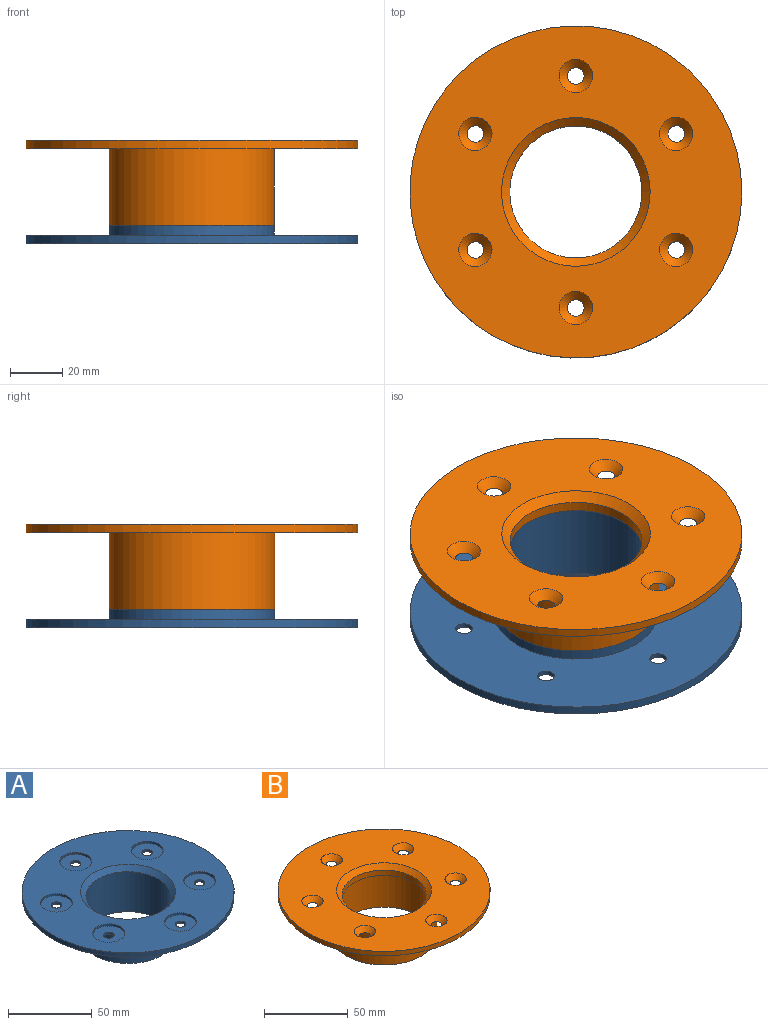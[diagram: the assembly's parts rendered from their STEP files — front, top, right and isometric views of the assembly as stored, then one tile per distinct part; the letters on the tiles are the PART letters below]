
ASSEMBLY  parts=2 mates=1
PART A: 27 faces, bbox 126.5x126.5x32.4 mm
  f0: cylinder r=3.17mm len=6.35mm, axis (0,0,-1), area 31.7mm2, adj f11,f25
  f1: cylinder r=3.17mm len=6.35mm, axis (0,0,-1), area 31.7mm2, adj f11,f15
  f2: cylinder r=3.17mm len=6.35mm, axis (0,0,-1), area 31.7mm2, adj f11,f17
  f3: cylinder r=3.17mm len=6.35mm, axis (0,0,-1), area 31.7mm2, adj f11,f19
  f4: cylinder r=3.17mm len=6.35mm, axis (0,0,-1), area 31.7mm2, adj f11,f21
  f5: cylinder r=3.17mm len=6.35mm, axis (0,0,-1), area 31.7mm2, adj f11,f23
  f6: cylinder r=31.5mm len=62.99mm, axis (0,0,1), area 754mm2, adj f11,f13
  f7: plane 56.64x56.64mm, normal (0,0,-1), area 533.3mm2, adj f8,f12
  f8: cylinder r=25.15mm len=50.29mm, axis (0,0,-1), area 4615.1mm2, adj f7,f26
  f9: cylinder r=63.25mm len=126.49mm, axis (0,0,-1), area 1261.7mm2, adj f10,f11
  f10: plane 126.49x126.49mm, normal (0,0,1), area 8336.6mm2, adj f9,f14,f16,f18,f20,f22,f24,f26
  f11: plane 126.49x126.49mm, normal (0,0,-1), area 9260.1mm2, adj f0,f1,f2,f3,f4,f5,f6,f9
  f12: cylinder r=28.32mm len=56.64mm, axis (0,0,-1), area 4519.8mm2, adj f7,f13
  f13: plane 62.99x62.99mm, normal (0,0,-1), area 596.6mm2, adj f6,f12
  f14: cylinder r=9.53mm len=19.05mm, axis (0,0,1), area 95mm2, adj f10,f15
  f15: plane 19.05x19.05mm, normal (0,0,1), area 253.4mm2, adj f1,f14
  f16: cylinder r=9.53mm len=19.05mm, axis (0,0,1), area 95mm2, adj f10,f17
  f17: plane 19.05x19.05mm, normal (0,0,1), area 253.4mm2, adj f2,f16
  f18: cylinder r=9.53mm len=19.05mm, axis (0,0,1), area 95mm2, adj f10,f19
  f19: plane 19.05x19.05mm, normal (0,0,1), area 253.4mm2, adj f3,f18
  f20: cylinder r=9.53mm len=19.05mm, axis (0,0,1), area 95mm2, adj f10,f21
  f21: plane 19.05x19.05mm, normal (0,0,1), area 253.4mm2, adj f4,f20
  f22: cylinder r=9.53mm len=19.05mm, axis (0,0,1), area 95mm2, adj f10,f23
  f23: plane 19.05x19.05mm, normal (0,0,1), area 253.4mm2, adj f5,f22
  f24: cylinder r=9.53mm len=19.05mm, axis (0,0,1), area 95mm2, adj f10,f25
  f25: plane 19.05x19.05mm, normal (0,0,1), area 253.4mm2, adj f0,f24
  f26: cone r=25.15mm half-angle=45deg, axis (0,0,1), area 754.2mm2, adj f8,f10
PART B: 15 faces, bbox 126.5x126.5x32.4 mm
  f0: cylinder r=25.15mm len=50.29mm, axis (0,0,-1), area 602mm2, adj f13,f14
  f1: cylinder r=63.25mm len=126.49mm, axis (0,0,-1), area 1261.7mm2, adj f2,f3
  f2: plane 126.49x126.49mm, normal (0,0,1), area 9286.7mm2, adj f1,f4,f5,f6,f7,f8,f9,f14
  f3: plane 126.49x126.49mm, normal (0,0,-1), area 9260.1mm2, adj f1,f4,f5,f6,f7,f8,f9,f10
  f4: cone r=3.17mm half-angle=45deg, axis (0,0,1), area 134.4mm2, adj f2,f3
  f5: cone r=3.17mm half-angle=45deg, axis (0,0,1), area 134.4mm2, adj f2,f3
  f6: cone r=3.17mm half-angle=45deg, axis (0,0,1), area 134.4mm2, adj f2,f3
  f7: cone r=3.17mm half-angle=45deg, axis (0,0,1), area 134.4mm2, adj f2,f3
  f8: cone r=3.17mm half-angle=45deg, axis (0,0,1), area 134.4mm2, adj f2,f3
  f9: cone r=3.17mm half-angle=45deg, axis (0,0,1), area 134.4mm2, adj f2,f3
  f10: cylinder r=31.5mm len=62.99mm, axis (0,0,1), area 5780.5mm2, adj f3,f11
  f11: plane 62.99x62.99mm, normal (0,0,-1), area 596.6mm2, adj f10,f12
  f12: cylinder r=28.32mm len=56.64mm, axis (0,0,-1), area 4519.8mm2, adj f11,f13
  f13: plane 56.64x56.64mm, normal (0,0,-1), area 533.3mm2, adj f0,f12
  f14: cone r=25.15mm half-angle=45deg, axis (0,0,1), area 754.2mm2, adj f0,f2
PLACE A rot(axis=(1,0,0),180deg) t=(-18.36,-8.69,-17.13)mm
PLACE B t=(-18.36,-8.69,15.89)mm
MATE fastened A.f6 <-> B.f10  axis (0,0,1) through (-18.36,-8.69,12.08)mm
